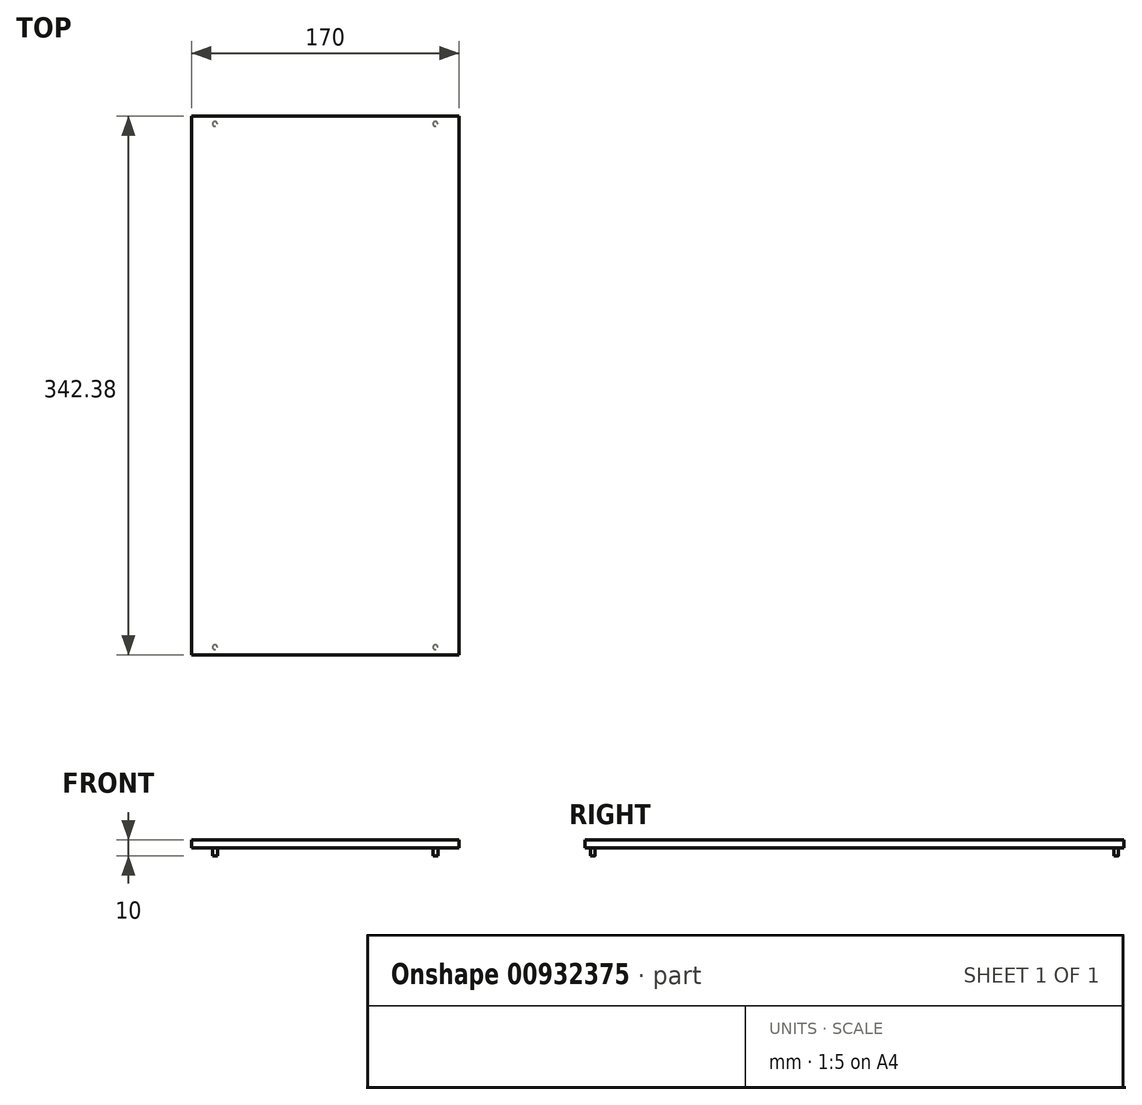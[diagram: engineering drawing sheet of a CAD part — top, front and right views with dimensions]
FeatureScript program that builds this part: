
annotation { "Feature Type Name" : "Feature", "Feature Type Description" : "" }
export const myFeature = defineFeature(function(context is Context, id is Id, definition is map)
    precondition{}
    {
        {
            var Q0;
            Q0=qCreatedBy(makeId("Top.planeOp"),FACE);
            var sketch = newSketch(context, id + "F0", { "sketchPlane" : qUnion([Q0])});
            skLineSegment(sketch, "E0.bottom", {"start": v(-85, -171.19) * mm, "end": v(85, -171.19) * mm});
            skLineSegment(sketch, "E0.top", {"start": v(-85, 171.19) * mm, "end": v(85, 171.19) * mm});
            skLineSegment(sketch, "E0.left", {"start": v(-85, -171.19) * mm, "end": v(-85, 171.19) * mm});
            skLineSegment(sketch, "E0.right", {"start": v(85, -171.19) * mm, "end": v(85, 171.19) * mm});
            skPoint(sketch, "E0.middle", {"position": v(0, 0) * mm});
            skSolve(sketch);
        }
        {
            var Q0;
            Q0=makeQuery(id+"F0.imprint","IMPRINT",FACE,{"disambiguationData":[TD([[makeQuery(id+"F0.imprint","IMPRINT",EDGE,{"derivedFrom":sQuery(id+"F0.wireOp",EDGE,"E0.bottom")}),1.0]])]});
            extrude(context, id + "F1", {"entities" : qUnion([Q0]), "depth" : 5 * mm, "offsetDistance" : 25 * mm});
        }
        {
            var Q0;
            Q0=qCreatedBy(makeId("Top.planeOp"),FACE);
            var sketch = newSketch(context, id + "F2", { "sketchPlane" : qUnion([Q0])});
            skCircle(sketch, "E1", {"center": v(70, -166.19) * mm, "radius": 1.5 * mm});
            skCircle(sketch, "E2.MirrorC", {"center": v(-70, -166.19) * mm, "radius": 1.5 * mm});
            skCircle(sketch, "E3.MirrorC", {"center": v(70, 166.19) * mm, "radius": 1.5 * mm});
            skCircle(sketch, "E4.MirrorC", {"center": v(-70, 166.19) * mm, "radius": 1.5 * mm});
            skSolve(sketch);
        }
        {
            var Q0;
            Q0 = qSketchRegion(id + "F2", true);
            extrude(context, id + "F3", {"entities" : qUnion([Q0]), "operationType" : NewBodyOperationType.ADD, "oppositeDirection" : true, "depth" : 5 * mm, "offsetDistance" : 25 * mm});
        }
    });
